# Revit family: Toilet-Floor_Mount-KOHLER-Juvenile-K-96059
name_source: partatom
category: Plumbing Fixtures
revit_build: Autodesk Revit 2015 (Build: 20140606_1530(x64)
units: mm (PartAtom-declared; Revit-internal decimal feet)

## types (2) — shared parameters
ADA Compliant = Yes
Assembly Code = D2010100
CW Connection = Yes
Cold Water Inlet = Cold Water Inlet
Date Modified = 10/13/2018
Default Elevation = 0"
Finish = Kohler-Vitreous_China-0-White
Flow Rate = 25 GPM
Flush Rate = 1.6 GPF
HW Connection = No
Height = 13 3/4"
Hot Water Inlet = Hot Water Inlet
Length = 25 15/16"
Manufacturer = KOHLER Co.
MasterFormat 1995 = 15410
MasterFormat 2004 = 22.41.13
Material = Vitreous China
Pressure = 80.00 psi
Product Documentation Link = http://www.us.kohler.com
Product Name = Juvenile
Product Page URL = http://www.us.kohler.com
Seat Included = No
URL = https://www.us.kohler.com
Vent Connection = No
Waste Connection = Yes
Waste Water Outlet = Waste Water Outlet
Width = 14 5/8"

## per-type parameters (varying)
| type | Description | Model | Type |
| 0 - White | Ultra flushometer bowl with top spud | K-96059-0 | 1 |
| Antimicrobial Finish, 0 - White | Ultra flushometer bowl with top spud, antimicrobial finish | K-96059-SS-0 | 2 |

## geometry (parser evidence)
native form markers: Sweep x5
no freeform markers — native parametric forms only
